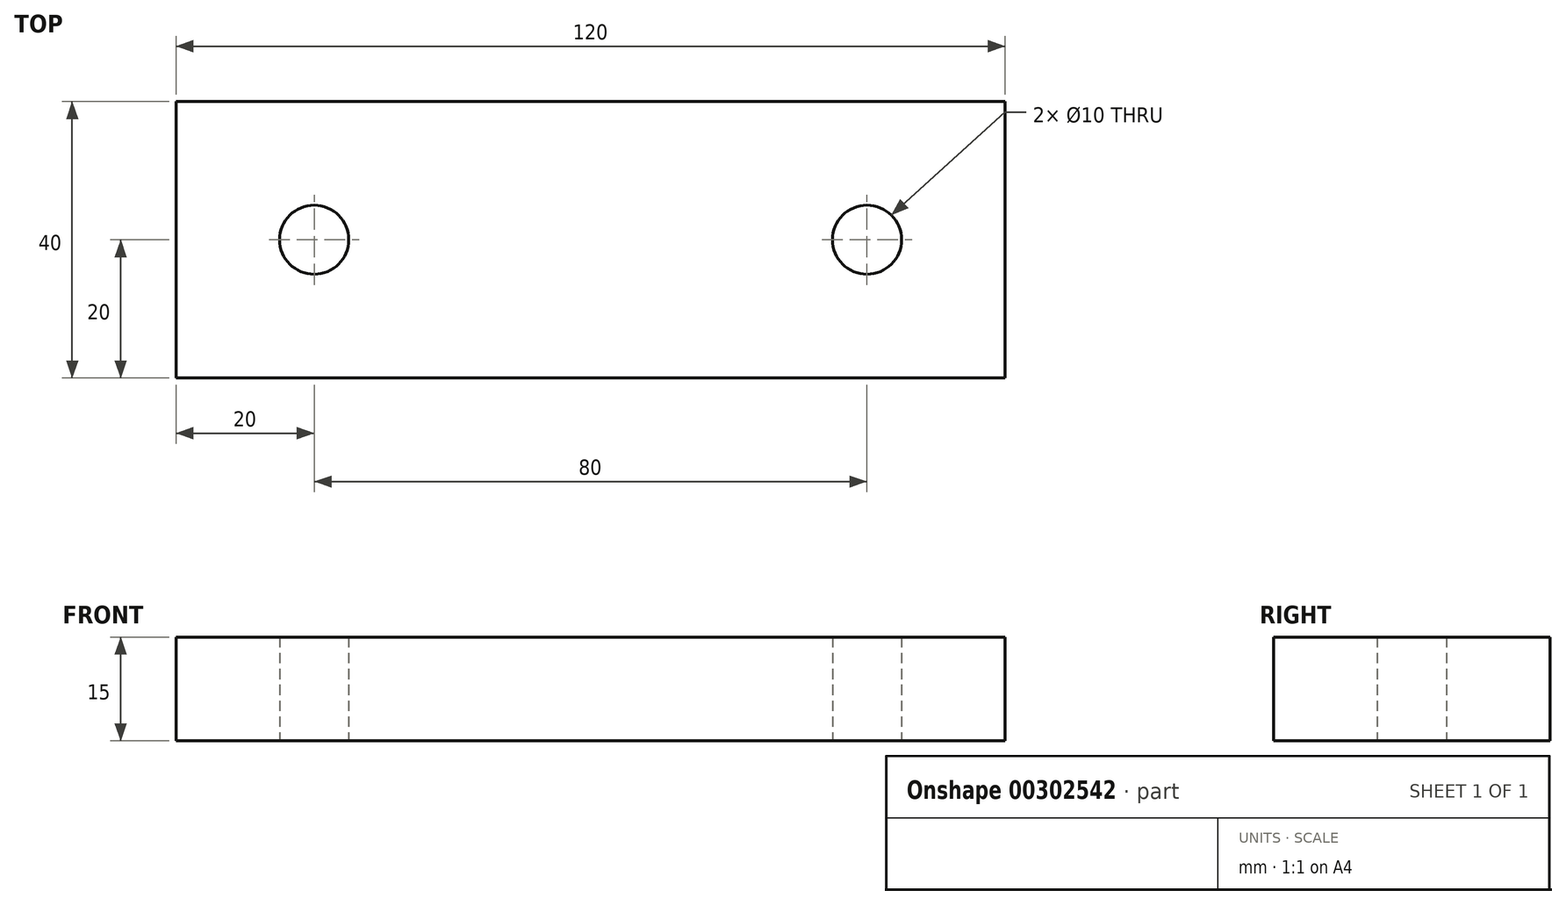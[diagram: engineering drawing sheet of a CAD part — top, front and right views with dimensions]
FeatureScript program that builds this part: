
annotation { "Feature Type Name" : "Feature", "Feature Type Description" : "" }
export const myFeature = defineFeature(function(context is Context, id is Id, definition is map)
    precondition{}
    {
        {
            var Q0;
            Q0=qCreatedBy(makeId("Top.planeOp"),FACE);
            var sketch = newSketch(context, id + "F0", { "sketchPlane" : qUnion([Q0])});
            skLineSegment(sketch, "E0", {"start": v(0, 0) * mm, "end": v(0, 40) * mm});
            skLineSegment(sketch, "E1", {"start": v(0, 40) * mm, "end": v(120, 40) * mm});
            skLineSegment(sketch, "E2", {"start": v(120, 40) * mm, "end": v(120, 0) * mm});
            skLineSegment(sketch, "E3", {"start": v(120, 0) * mm, "end": v(0, 0) * mm});
            skCircle(sketch, "E4", {"center": v(20, 20) * mm, "radius": 5 * mm});
            skCircle(sketch, "E5", {"center": v(100, 20) * mm, "radius": 5 * mm});
            skSolve(sketch);
        }
        {
            var Q0;
            Q0=makeQuery(id+"F0.imprint","IMPRINT",FACE,{"disambiguationData":[TD([[makeQuery(id+"F0.imprint","IMPRINT",EDGE,{"derivedFrom":sQuery(id+"F0.wireOp",EDGE,"E0")}),-1.0]])]});
            extrude(context, id + "F1", {"entities" : qUnion([Q0]), "depth" : 15 * mm});
        }
    });
